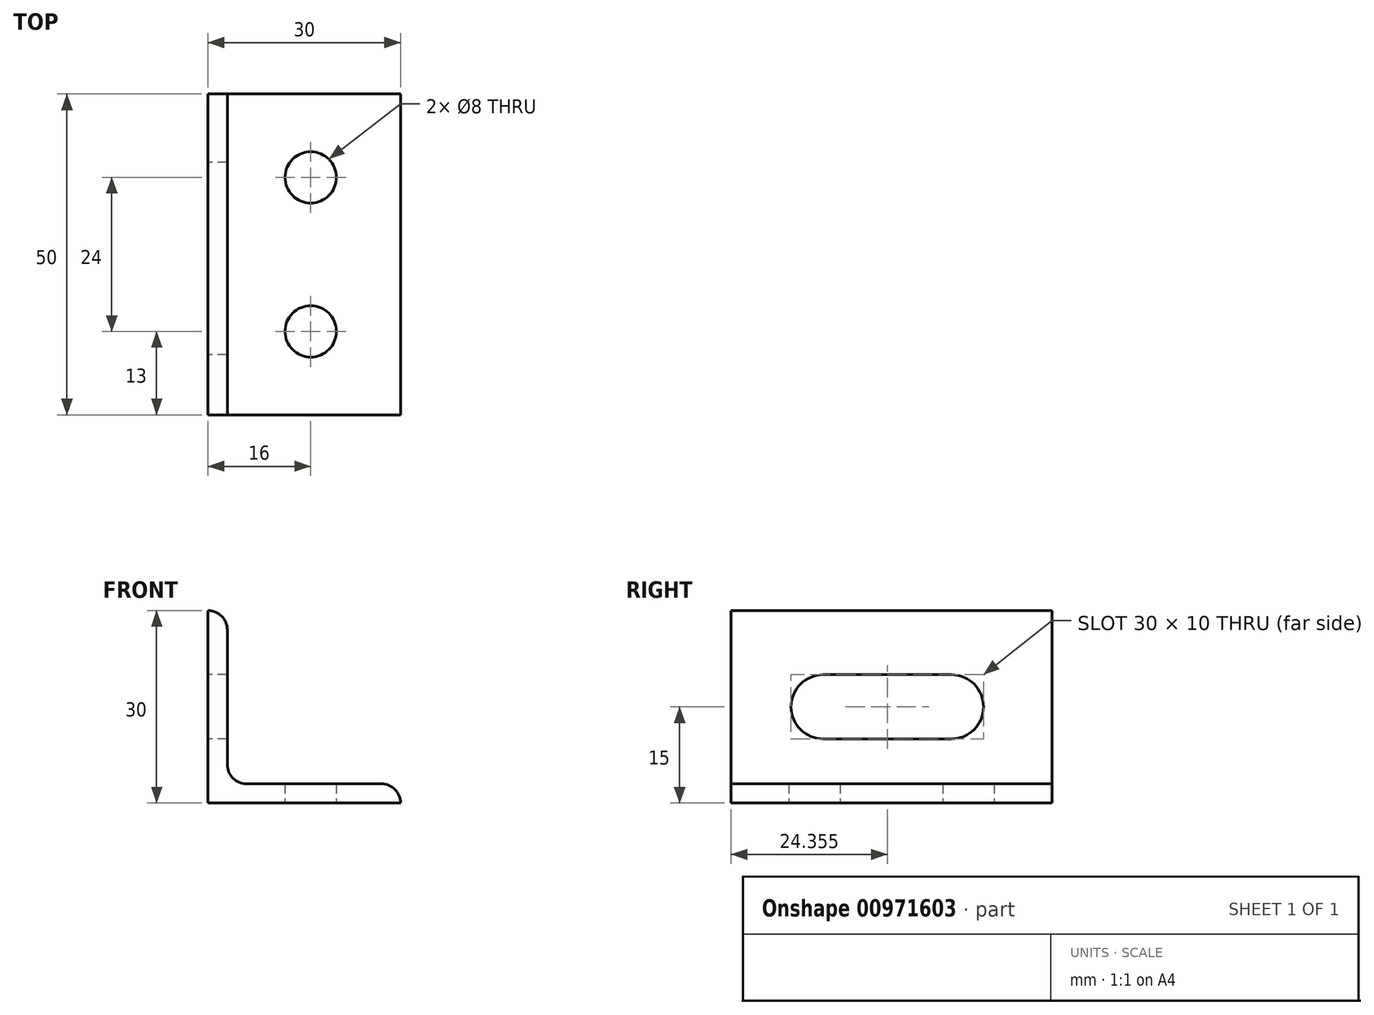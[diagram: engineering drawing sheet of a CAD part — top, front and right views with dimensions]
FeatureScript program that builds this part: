
annotation { "Feature Type Name" : "Feature", "Feature Type Description" : "" }
export const myFeature = defineFeature(function(context is Context, id is Id, definition is map)
    precondition{}
    {
        {
            var Q0;
            Q0=qCreatedBy(makeId("Front.planeOp"),FACE);
            var sketch = newSketch(context, id + "F0", { "sketchPlane" : qUnion([Q0])});
            skLineSegment(sketch, "E0", {"start": v(0, 0) * mm, "end": v(30, 0) * mm});
            skLineSegment(sketch, "E1", {"start": v(30, 0) * mm, "end": v(30, 0) * mm});
            skLineSegment(sketch, "E2", {"start": v(27, 3) * mm, "end": v(6, 3) * mm});
            skLineSegment(sketch, "E3", {"start": v(3, 6) * mm, "end": v(3, 27) * mm});
            skLineSegment(sketch, "E4", {"start": v(0, 30) * mm, "end": v(0, 30) * mm});
            skLineSegment(sketch, "E5", {"start": v(0, 30) * mm, "end": v(0, 0) * mm});
            skPoint(sketch, "E6.visualSharp", {"position": v(3, 3) * mm});
            skArc(sketch, "E6.filletArc", {"start": v(3, 6) * mm, "mid": v(3.88, 3.88) * mm, "end": v(6, 3) * mm});
            skPoint(sketch, "E7.visualSharp", {"position": v(3, 30) * mm});
            skArc(sketch, "E7.filletArc", {"start": v(3, 27) * mm, "mid": v(2.12, 29.12) * mm, "end": v(0, 30) * mm});
            skPoint(sketch, "E8.visualSharp", {"position": v(30, 3) * mm});
            skArc(sketch, "E8.filletArc", {"start": v(30, 0) * mm, "mid": v(29.12, 2.12) * mm, "end": v(27, 3) * mm});
            skSolve(sketch);
        }
        {
            var Q0;
            Q0 = qSketchRegion(id + "F0", true);
            extrude(context, id + "F1", {"entities" : qUnion([Q0]), "depth" : 25 * mm, "offsetDistance" : 25 * mm, "hasSecondDirection" : true, "secondDirectionOppositeDirection" : true, "secondDirectionDepth" : 25 * mm});
        }
        {
            var Q0;
            Q0=qCreatedBy(makeId("Top.planeOp"),FACE);
            var sketch = newSketch(context, id + "F2", { "sketchPlane" : qUnion([Q0])});
            skCircle(sketch, "E9", {"center": v(16, -12) * mm, "radius": 4 * mm});
            skCircle(sketch, "E10", {"center": v(16, 12) * mm, "radius": 4 * mm});
            skSolve(sketch);
        }
        {
            var Q0;
            Q0 = qSketchRegion(id + "F2", true);
            extrude(context, id + "F3", {"entities" : qUnion([Q0]), "operationType" : NewBodyOperationType.REMOVE, "depth" : 25 * mm, "offsetDistance" : 25 * mm});
        }
        {
            var Q0;
            Q0=makeQuery(id+"F1.opExtrude","SWEPT_FACE",FACE,{"disambiguationData":[OSD([sQuery(id+"F0.wireOp",EDGE,"E5")])]});
            var sketch = newSketch(context, id + "F4", { "sketchPlane" : qUnion([Q0])});
            skLineSegment(sketch, "E11", {"start": v(-9.36, 15) * mm, "end": v(10.64, 15) * mm});
            skSolve(sketch);
        }
        {
            var Q0;
            {var subQ0=sQuery(id+"F0.wireOp",EDGE,"E5");Q0=makeQuery(id+"F4.imprint","IMPRINT",FACE,{"disambiguationData":[TD([[makeQuery(id+"F4.imprint","IMPRINT",EDGE,{"derivedFrom":makeQuery(id+"F1.opExtrude","CAP_EDGE",EDGE,{"disambiguationData":[OSD([subQ0])],"isStart":true})}),1.0]])]});}
            var sketch = newSketch(context, id + "F5", { "sketchPlane" : qUnion([Q0])});
            skLineSegment(sketch, "E12.JMB.JMB", {"start": v(-9.36, 15) * mm, "end": v(10.64, 15) * mm, "construction": true});
            skArc(sketch, "E12.0.startCap", {"start": v(-9.36, 10) * mm, "mid": v(-14.36, 15) * mm, "end": v(-9.36, 20) * mm});
            skArc(sketch, "E12.0.endCap", {"start": v(10.64, 20) * mm, "mid": v(15.64, 15) * mm, "end": v(10.64, 10) * mm});
            skLineSegment(sketch, "E12.0.left", {"start": v(-9.36, 20) * mm, "end": v(10.64, 20) * mm});
            skLineSegment(sketch, "E12.0.right", {"start": v(-9.36, 10) * mm, "end": v(10.64, 10) * mm});
            skSolve(sketch);
        }
        {
            var Q0;
            Q0 = qSketchRegion(id + "F5", true);
            extrude(context, id + "F6", {"entities" : qUnion([Q0]), "operationType" : NewBodyOperationType.REMOVE, "oppositeDirection" : true, "depth" : 25 * mm, "offsetDistance" : 25 * mm});
        }
    });
